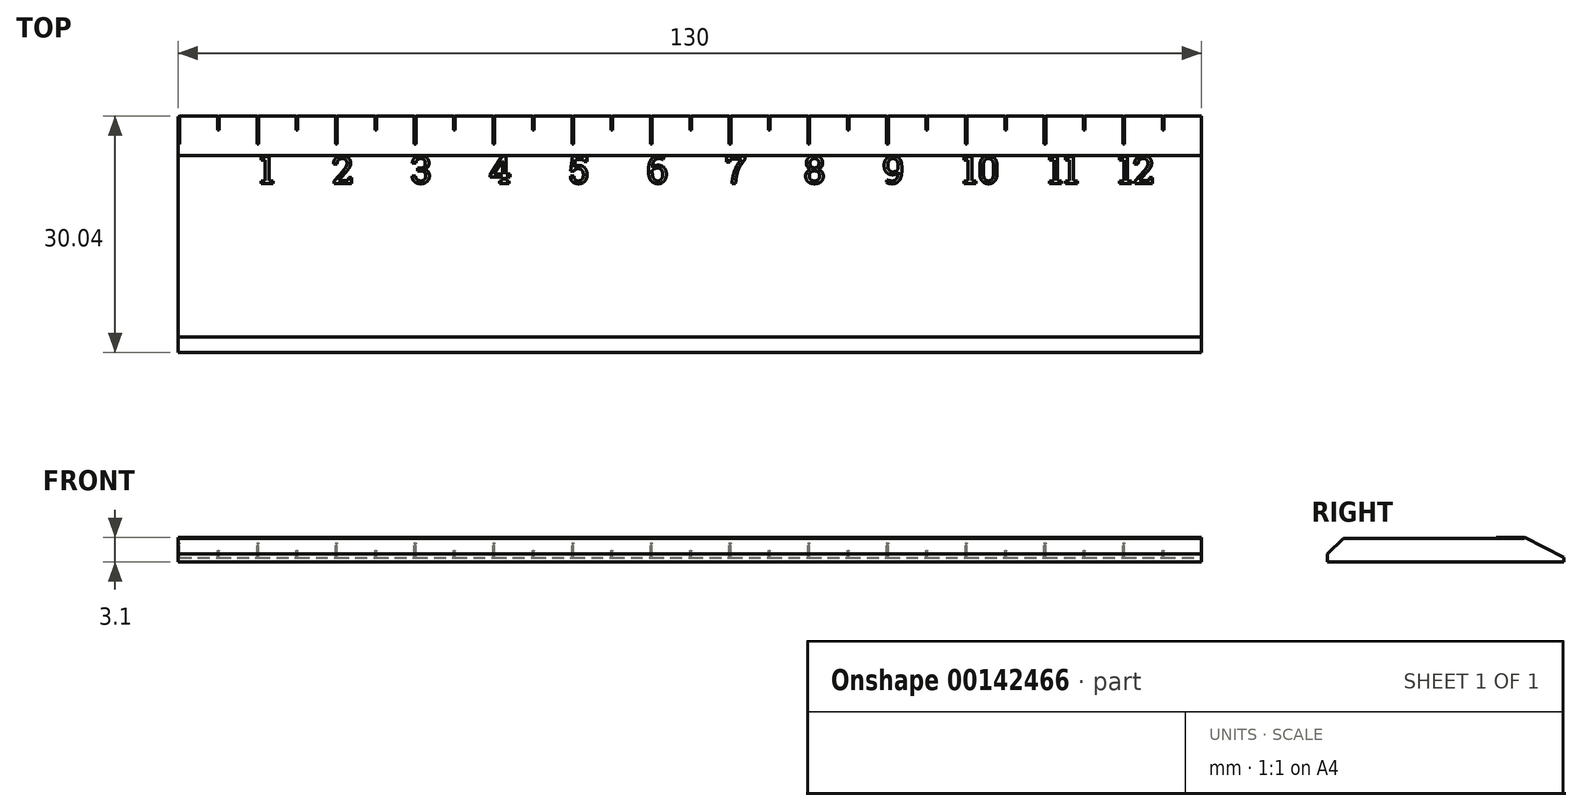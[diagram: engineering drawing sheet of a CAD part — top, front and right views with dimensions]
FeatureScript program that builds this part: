
annotation { "Feature Type Name" : "Feature", "Feature Type Description" : "" }
export const myFeature = defineFeature(function(context is Context, id is Id, definition is map)
    precondition{}
    {
        {
            var Q0;
            Q0=qCreatedBy(makeId("Top.planeOp"),FACE);
            var sketch = newSketch(context, id + "F0", { "sketchPlane" : qUnion([Q0])});
            skLineSegment(sketch, "E0.bottom", {"start": v(0, 0) * mm, "end": v(130, 0) * mm});
            skLineSegment(sketch, "E0.top", {"start": v(0, 30) * mm, "end": v(130, 30) * mm});
            skLineSegment(sketch, "E0.left", {"start": v(0, 0) * mm, "end": v(0, 30) * mm});
            skLineSegment(sketch, "E0.right", {"start": v(130, 0) * mm, "end": v(130, 30) * mm});
            skSolve(sketch);
        }
        {
            var Q0;
            Q0=makeQuery(id+"F0.imprint","IMPRINT",FACE,{"disambiguationData":[TD([[makeQuery(id+"F0.imprint","IMPRINT",EDGE,{"derivedFrom":sQuery(id+"F0.wireOp",EDGE,"E0.bottom")}),1.0]])]});
            extrude(context, id + "F1", {"entities" : qUnion([Q0]), "depth" : 3 * mm});
        }
        {
            var Q0;
            Q0=makeQuery(id+"F1.opExtrude","CAP_EDGE",EDGE,{"disambiguationData":[OSD([sQuery(id+"F0.wireOp",EDGE,"E0.top")])],"isStart":false});
            chamfer(context, id + "F2", {"entities" : qUnion([Q0]), "chamferType" : ChamferType.TWO_OFFSETS, "width1" : 2.5 * mm, "oppositeDirection" : false, "width2" : 5 * mm, "tangentPropagation" : true});
        }
        {
            var Q0;
            Q0=makeQuery(id+"F1.opExtrude","CAP_EDGE",EDGE,{"disambiguationData":[OSD([sQuery(id+"F0.wireOp",EDGE,"E0.bottom")])],"isStart":false});
            chamfer(context, id + "F3", {"entities" : qUnion([Q0]), "chamferType" : ChamferType.TWO_OFFSETS, "width1" : 2 * mm, "oppositeDirection" : false, "width2" : 2 * mm, "tangentPropagation" : true});
        }
        {
            var Q0;
            Q0=makeQuery(id+"F2.opChamfer","BLEND_FACE",FACE,{"disambiguationData":[OSD([sQuery(id+"F0.wireOp",EDGE,"E0.top")])]});
            var sketch = newSketch(context, id + "F4", { "sketchPlane" : qUnion([Q0])});
            skLineSegment(sketch, "E1.bottom", {"start": v(0, 26.6) * mm, "end": v(0.2, 26.6) * mm});
            skLineSegment(sketch, "E1.top", {"start": v(0, 22.6) * mm, "end": v(0.2, 22.6) * mm});
            skLineSegment(sketch, "E1.left", {"start": v(0, 26.6) * mm, "end": v(0, 22.6) * mm});
            skLineSegment(sketch, "E1.right", {"start": v(0.2, 26.6) * mm, "end": v(0.2, 22.6) * mm});
            skLineSegment(sketch, "E2.1.0.0", {"start": v(10, 26.6) * mm, "end": v(10, 22.6) * mm});
            skLineSegment(sketch, "E2.1.0.1", {"start": v(10.2, 26.6) * mm, "end": v(10.2, 22.6) * mm});
            skLineSegment(sketch, "E2.1.0.2", {"start": v(10, 22.6) * mm, "end": v(10.2, 22.6) * mm});
            skLineSegment(sketch, "E2.1.0.3", {"start": v(10, 26.6) * mm, "end": v(10.2, 26.6) * mm});
            skLineSegment(sketch, "E2.2.0.0", {"start": v(20, 26.6) * mm, "end": v(20, 22.6) * mm});
            skLineSegment(sketch, "E2.2.0.1", {"start": v(20.2, 26.6) * mm, "end": v(20.2, 22.6) * mm});
            skLineSegment(sketch, "E2.2.0.2", {"start": v(20, 22.6) * mm, "end": v(20.2, 22.6) * mm});
            skLineSegment(sketch, "E2.2.0.3", {"start": v(20, 26.6) * mm, "end": v(20.2, 26.6) * mm});
            skLineSegment(sketch, "E2.3.0.0", {"start": v(30, 26.6) * mm, "end": v(30, 22.6) * mm});
            skLineSegment(sketch, "E2.3.0.1", {"start": v(30.2, 26.6) * mm, "end": v(30.2, 22.6) * mm});
            skLineSegment(sketch, "E2.3.0.2", {"start": v(30, 22.6) * mm, "end": v(30.2, 22.6) * mm});
            skLineSegment(sketch, "E2.3.0.3", {"start": v(30, 26.6) * mm, "end": v(30.2, 26.6) * mm});
            skLineSegment(sketch, "E2.4.0.0", {"start": v(40, 26.6) * mm, "end": v(40, 22.6) * mm});
            skLineSegment(sketch, "E2.4.0.1", {"start": v(40.2, 26.6) * mm, "end": v(40.2, 22.6) * mm});
            skLineSegment(sketch, "E2.4.0.2", {"start": v(40, 22.6) * mm, "end": v(40.2, 22.6) * mm});
            skLineSegment(sketch, "E2.4.0.3", {"start": v(40, 26.6) * mm, "end": v(40.2, 26.6) * mm});
            skLineSegment(sketch, "E2.5.0.0", {"start": v(50, 26.6) * mm, "end": v(50, 22.6) * mm});
            skLineSegment(sketch, "E2.5.0.1", {"start": v(50.2, 26.6) * mm, "end": v(50.2, 22.6) * mm});
            skLineSegment(sketch, "E2.5.0.2", {"start": v(50, 22.6) * mm, "end": v(50.2, 22.6) * mm});
            skLineSegment(sketch, "E2.5.0.3", {"start": v(50, 26.6) * mm, "end": v(50.2, 26.6) * mm});
            skLineSegment(sketch, "E2.6.0.0", {"start": v(60, 26.6) * mm, "end": v(60, 22.6) * mm});
            skLineSegment(sketch, "E2.6.0.1", {"start": v(60.2, 26.6) * mm, "end": v(60.2, 22.6) * mm});
            skLineSegment(sketch, "E2.6.0.2", {"start": v(60, 22.6) * mm, "end": v(60.2, 22.6) * mm});
            skLineSegment(sketch, "E2.6.0.3", {"start": v(60, 26.6) * mm, "end": v(60.2, 26.6) * mm});
            skLineSegment(sketch, "E2.7.0.0", {"start": v(70, 26.6) * mm, "end": v(70, 22.6) * mm});
            skLineSegment(sketch, "E2.7.0.1", {"start": v(70.2, 26.6) * mm, "end": v(70.2, 22.6) * mm});
            skLineSegment(sketch, "E2.7.0.2", {"start": v(70, 22.6) * mm, "end": v(70.2, 22.6) * mm});
            skLineSegment(sketch, "E2.7.0.3", {"start": v(70, 26.6) * mm, "end": v(70.2, 26.6) * mm});
            skLineSegment(sketch, "E2.8.0.0", {"start": v(80, 26.6) * mm, "end": v(80, 22.6) * mm});
            skLineSegment(sketch, "E2.8.0.1", {"start": v(80.2, 26.6) * mm, "end": v(80.2, 22.6) * mm});
            skLineSegment(sketch, "E2.8.0.2", {"start": v(80, 22.6) * mm, "end": v(80.2, 22.6) * mm});
            skLineSegment(sketch, "E2.8.0.3", {"start": v(80, 26.6) * mm, "end": v(80.2, 26.6) * mm});
            skLineSegment(sketch, "E2.9.0.0", {"start": v(90, 26.6) * mm, "end": v(90, 22.6) * mm});
            skLineSegment(sketch, "E2.9.0.1", {"start": v(90.2, 26.6) * mm, "end": v(90.2, 22.6) * mm});
            skLineSegment(sketch, "E2.9.0.2", {"start": v(90, 22.6) * mm, "end": v(90.2, 22.6) * mm});
            skLineSegment(sketch, "E2.9.0.3", {"start": v(90, 26.6) * mm, "end": v(90.2, 26.6) * mm});
            skLineSegment(sketch, "E2.10.0.0", {"start": v(100, 26.6) * mm, "end": v(100, 22.6) * mm});
            skLineSegment(sketch, "E2.10.0.1", {"start": v(100.2, 26.6) * mm, "end": v(100.2, 22.6) * mm});
            skLineSegment(sketch, "E2.10.0.2", {"start": v(100, 22.6) * mm, "end": v(100.2, 22.6) * mm});
            skLineSegment(sketch, "E2.10.0.3", {"start": v(100, 26.6) * mm, "end": v(100.2, 26.6) * mm});
            skLineSegment(sketch, "E2.11.0.0", {"start": v(110, 26.6) * mm, "end": v(110, 22.6) * mm});
            skLineSegment(sketch, "E2.11.0.1", {"start": v(110.2, 26.6) * mm, "end": v(110.2, 22.6) * mm});
            skLineSegment(sketch, "E2.11.0.2", {"start": v(110, 22.6) * mm, "end": v(110.2, 22.6) * mm});
            skLineSegment(sketch, "E2.11.0.3", {"start": v(110, 26.6) * mm, "end": v(110.2, 26.6) * mm});
            skLineSegment(sketch, "E2.12.0.0", {"start": v(120, 26.6) * mm, "end": v(120, 22.6) * mm});
            skLineSegment(sketch, "E2.12.0.1", {"start": v(120.2, 26.6) * mm, "end": v(120.2, 22.6) * mm});
            skLineSegment(sketch, "E2.12.0.2", {"start": v(120, 22.6) * mm, "end": v(120.2, 22.6) * mm});
            skLineSegment(sketch, "E2.12.0.3", {"start": v(120, 26.6) * mm, "end": v(120.2, 26.6) * mm});
            skLineSegment(sketch, "E2.13.0.0", {"start": v(130, 26.6) * mm, "end": v(130, 22.6) * mm});
            skLineSegment(sketch, "E2.13.0.1", {"start": v(130.2, 26.6) * mm, "end": v(130.2, 22.6) * mm});
            skLineSegment(sketch, "E2.13.0.2", {"start": v(130, 22.6) * mm, "end": v(130.2, 22.6) * mm});
            skLineSegment(sketch, "E2.13.0.3", {"start": v(130, 26.6) * mm, "end": v(130.2, 26.6) * mm});
            skLineSegment(sketch, "E2.direction1", {"start": v(0, 22.6) * mm, "end": v(10, 22.6) * mm, "construction": true});
            skLineSegment(sketch, "E3.bottom", {"start": v(5, 26.6) * mm, "end": v(5.2, 26.6) * mm});
            skLineSegment(sketch, "E3.top", {"start": v(5, 24.6) * mm, "end": v(5.2, 24.6) * mm});
            skLineSegment(sketch, "E3.left", {"start": v(5, 26.6) * mm, "end": v(5, 24.6) * mm});
            skLineSegment(sketch, "E3.right", {"start": v(5.2, 26.6) * mm, "end": v(5.2, 24.6) * mm});
            skLineSegment(sketch, "E4.1.0.0", {"start": v(15, 26.6) * mm, "end": v(15, 24.6) * mm});
            skLineSegment(sketch, "E4.1.0.1", {"start": v(15.2, 26.6) * mm, "end": v(15.2, 24.6) * mm});
            skLineSegment(sketch, "E4.1.0.2", {"start": v(15, 24.6) * mm, "end": v(15.2, 24.6) * mm});
            skLineSegment(sketch, "E4.1.0.3", {"start": v(15, 26.6) * mm, "end": v(15.2, 26.6) * mm});
            skLineSegment(sketch, "E4.2.0.0", {"start": v(25, 26.6) * mm, "end": v(25, 24.6) * mm});
            skLineSegment(sketch, "E4.2.0.1", {"start": v(25.2, 26.6) * mm, "end": v(25.2, 24.6) * mm});
            skLineSegment(sketch, "E4.2.0.2", {"start": v(25, 24.6) * mm, "end": v(25.2, 24.6) * mm});
            skLineSegment(sketch, "E4.2.0.3", {"start": v(25, 26.6) * mm, "end": v(25.2, 26.6) * mm});
            skLineSegment(sketch, "E4.3.0.0", {"start": v(35, 26.6) * mm, "end": v(35, 24.6) * mm});
            skLineSegment(sketch, "E4.3.0.1", {"start": v(35.2, 26.6) * mm, "end": v(35.2, 24.6) * mm});
            skLineSegment(sketch, "E4.3.0.2", {"start": v(35, 24.6) * mm, "end": v(35.2, 24.6) * mm});
            skLineSegment(sketch, "E4.3.0.3", {"start": v(35, 26.6) * mm, "end": v(35.2, 26.6) * mm});
            skLineSegment(sketch, "E4.4.0.0", {"start": v(45, 26.6) * mm, "end": v(45, 24.6) * mm});
            skLineSegment(sketch, "E4.4.0.1", {"start": v(45.2, 26.6) * mm, "end": v(45.2, 24.6) * mm});
            skLineSegment(sketch, "E4.4.0.2", {"start": v(45, 24.6) * mm, "end": v(45.2, 24.6) * mm});
            skLineSegment(sketch, "E4.4.0.3", {"start": v(45, 26.6) * mm, "end": v(45.2, 26.6) * mm});
            skLineSegment(sketch, "E4.5.0.0", {"start": v(55, 26.6) * mm, "end": v(55, 24.6) * mm});
            skLineSegment(sketch, "E4.5.0.1", {"start": v(55.2, 26.6) * mm, "end": v(55.2, 24.6) * mm});
            skLineSegment(sketch, "E4.5.0.2", {"start": v(55, 24.6) * mm, "end": v(55.2, 24.6) * mm});
            skLineSegment(sketch, "E4.5.0.3", {"start": v(55, 26.6) * mm, "end": v(55.2, 26.6) * mm});
            skLineSegment(sketch, "E4.6.0.0", {"start": v(65, 26.6) * mm, "end": v(65, 24.6) * mm});
            skLineSegment(sketch, "E4.6.0.1", {"start": v(65.2, 26.6) * mm, "end": v(65.2, 24.6) * mm});
            skLineSegment(sketch, "E4.6.0.2", {"start": v(65, 24.6) * mm, "end": v(65.2, 24.6) * mm});
            skLineSegment(sketch, "E4.6.0.3", {"start": v(65, 26.6) * mm, "end": v(65.2, 26.6) * mm});
            skLineSegment(sketch, "E4.7.0.0", {"start": v(75, 26.6) * mm, "end": v(75, 24.6) * mm});
            skLineSegment(sketch, "E4.7.0.1", {"start": v(75.2, 26.6) * mm, "end": v(75.2, 24.6) * mm});
            skLineSegment(sketch, "E4.7.0.2", {"start": v(75, 24.6) * mm, "end": v(75.2, 24.6) * mm});
            skLineSegment(sketch, "E4.7.0.3", {"start": v(75, 26.6) * mm, "end": v(75.2, 26.6) * mm});
            skLineSegment(sketch, "E4.8.0.0", {"start": v(85, 26.6) * mm, "end": v(85, 24.6) * mm});
            skLineSegment(sketch, "E4.8.0.1", {"start": v(85.2, 26.6) * mm, "end": v(85.2, 24.6) * mm});
            skLineSegment(sketch, "E4.8.0.2", {"start": v(85, 24.6) * mm, "end": v(85.2, 24.6) * mm});
            skLineSegment(sketch, "E4.8.0.3", {"start": v(85, 26.6) * mm, "end": v(85.2, 26.6) * mm});
            skLineSegment(sketch, "E4.9.0.0", {"start": v(95, 26.6) * mm, "end": v(95, 24.6) * mm});
            skLineSegment(sketch, "E4.9.0.1", {"start": v(95.2, 26.6) * mm, "end": v(95.2, 24.6) * mm});
            skLineSegment(sketch, "E4.9.0.2", {"start": v(95, 24.6) * mm, "end": v(95.2, 24.6) * mm});
            skLineSegment(sketch, "E4.9.0.3", {"start": v(95, 26.6) * mm, "end": v(95.2, 26.6) * mm});
            skLineSegment(sketch, "E4.10.0.0", {"start": v(105, 26.6) * mm, "end": v(105, 24.6) * mm});
            skLineSegment(sketch, "E4.10.0.1", {"start": v(105.2, 26.6) * mm, "end": v(105.2, 24.6) * mm});
            skLineSegment(sketch, "E4.10.0.2", {"start": v(105, 24.6) * mm, "end": v(105.2, 24.6) * mm});
            skLineSegment(sketch, "E4.10.0.3", {"start": v(105, 26.6) * mm, "end": v(105.2, 26.6) * mm});
            skLineSegment(sketch, "E4.11.0.0", {"start": v(115, 26.6) * mm, "end": v(115, 24.6) * mm});
            skLineSegment(sketch, "E4.11.0.1", {"start": v(115.2, 26.6) * mm, "end": v(115.2, 24.6) * mm});
            skLineSegment(sketch, "E4.11.0.2", {"start": v(115, 24.6) * mm, "end": v(115.2, 24.6) * mm});
            skLineSegment(sketch, "E4.11.0.3", {"start": v(115, 26.6) * mm, "end": v(115.2, 26.6) * mm});
            skLineSegment(sketch, "E4.12.0.0", {"start": v(125, 26.6) * mm, "end": v(125, 24.6) * mm});
            skLineSegment(sketch, "E4.12.0.1", {"start": v(125.2, 26.6) * mm, "end": v(125.2, 24.6) * mm});
            skLineSegment(sketch, "E4.12.0.2", {"start": v(125, 24.6) * mm, "end": v(125.2, 24.6) * mm});
            skLineSegment(sketch, "E4.12.0.3", {"start": v(125, 26.6) * mm, "end": v(125.2, 26.6) * mm});
            skLineSegment(sketch, "E4.direction1", {"start": v(5, 24.6) * mm, "end": v(15, 24.6) * mm, "construction": true});
            skSolve(sketch);
        }
        {
            var Q0;
            {var subQ44=sQuery(id+"F4.wireOp",EDGE,"E1.top");Q0=makeQuery(id+"F4.imprint","IMPRINT",FACE,{"disambiguationData":[TD([[makeQuery(id+"F4.imprint","IMPRINT",EDGE,{"derivedFrom":subQ44}),-1.0]])]});}
            extrude(context, id + "F5", {"entities" : qUnion([Q0]), "operationType" : NewBodyOperationType.ADD, "depth" : 0.1 * mm});
        }
        {
            var Q0;
            Q0=makeQuery(id+"F1.opExtrude","CAP_FACE",FACE,{"disambiguationData":[OSD([sQuery(id+"F0.wireOp",EDGE,"E0.bottom"),sQuery(id+"F0.wireOp",EDGE,"E0.top"),sQuery(id+"F0.wireOp",EDGE,"E0.left"),sQuery(id+"F0.wireOp",EDGE,"E0.right")])],"isStart":false});
            var sketch = newSketch(context, id + "F6", { "sketchPlane" : qUnion([Q0])});
            skText(sketch, "E5", { "text": "1      2      3      4      5      6      7      8      9      10     11    12", "fontName": "RobotoSlab-Regular.ttf"});
            const initialGuessF6  = {"E5": [0.01024, 0.02148, 1, 0, 0.00352]};
            skSetInitialGuess(sketch, initialGuessF6);
            skSolve(sketch);
        }
        {
            var Q0;
            Q0 = qSketchRegion(id + "F6", true);
            extrude(context, id + "F7", {"entities" : qUnion([Q0]), "operationType" : NewBodyOperationType.ADD, "depth" : 0.1 * mm});
        }
    });
